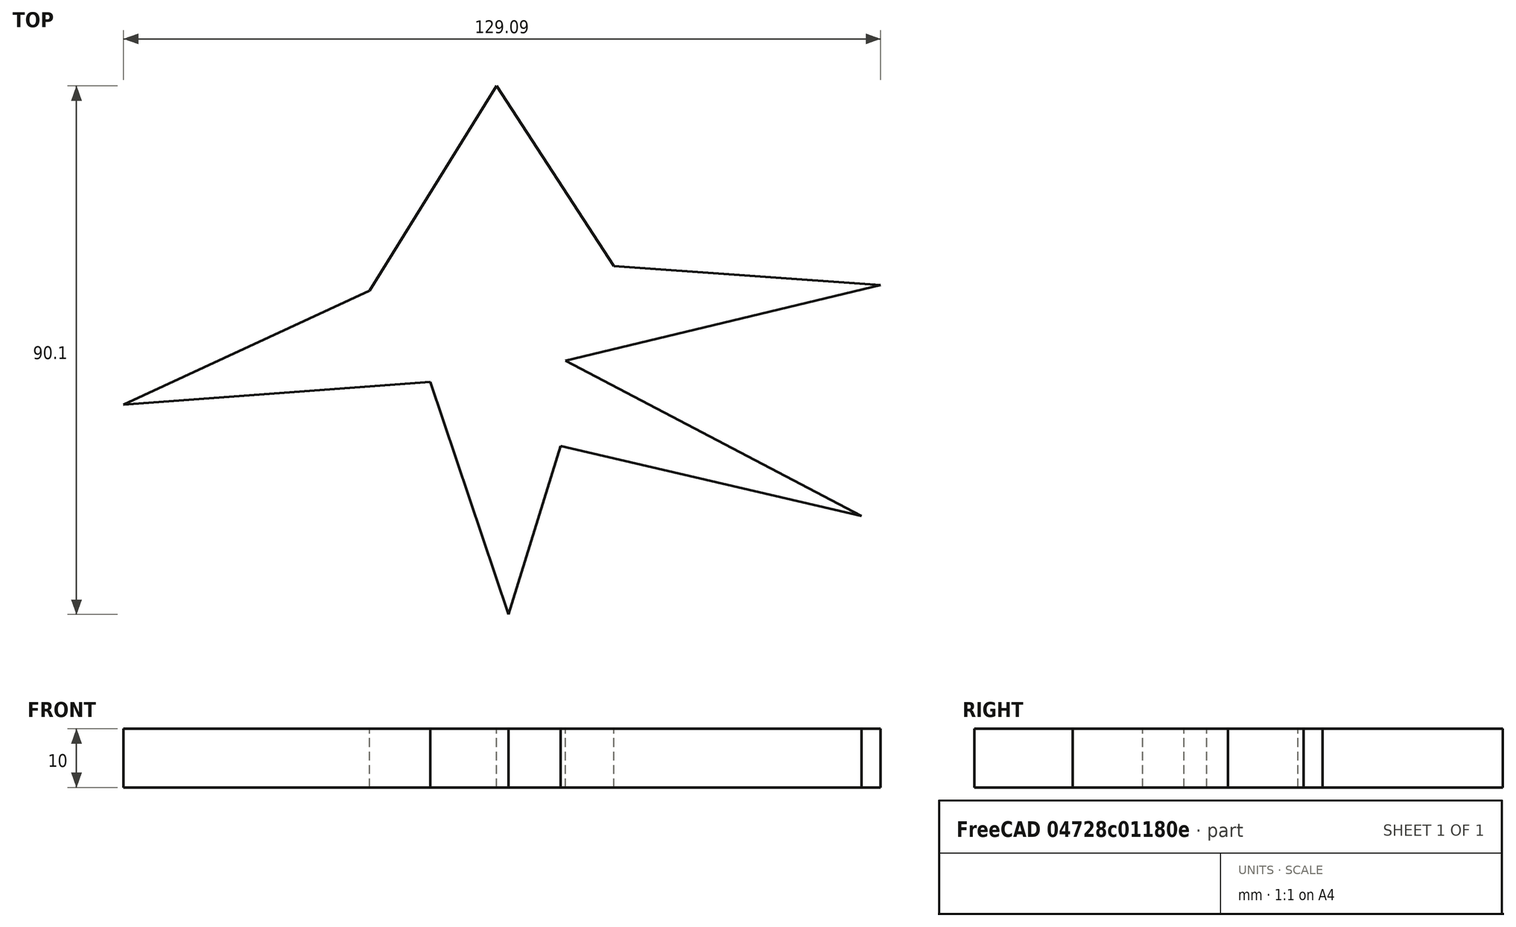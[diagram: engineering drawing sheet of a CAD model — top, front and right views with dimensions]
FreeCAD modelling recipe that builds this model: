
FCSTD DOCUMENT  (FreeCAD 0.21R33694 (Git))
Label: OJT1_T16P01_estrella
License: All rights reserved
LicenseURL: http://en.wikipedia.org/wiki/All_rights_reserved
objects: Sketcher::SketchObject×1, PartDesign::Pad×1, PartDesign::Body×1
note: 4 computed .brp shape members not serialized (recipe doc carries the construction recipe); baked Part::Feature solids carry a one-line shape summary decoded from their .brp

FEATURE [Sketcher::SketchObject] Sketch
  FullyConstrained = false
  MapMode = 5
  Support = -> [XY_Plane]
  sketch-geometry (11):
    g0: LineSegment StartX=-21.6998 StartY=9.21755 StartZ=0 EndX=0.000202475 EndY=44.1413 EndZ=0
    g1: LineSegment StartX=0.000202475 StartY=44.1413 StartZ=0 EndX=20 EndY=13.4343 EndZ=0
    g2: LineSegment StartX=20 StartY=13.4343 StartZ=0 EndX=65.4545 EndY=10.202 EndZ=0
    g3: LineSegment StartX=65.4545 StartY=10.202 StartZ=0 EndX=11.7172 EndY=-2.72727 EndZ=0
    g4: LineSegment StartX=11.7172 StartY=-2.72727 StartZ=0 EndX=62.2222 EndY=-29.1919 EndZ=0
    g5: LineSegment StartX=62.2222 StartY=-29.1919 StartZ=0 EndX=10.9091 EndY=-17.2727 EndZ=0
    g6: LineSegment StartX=10.9091 StartY=-17.2727 StartZ=0 EndX=2.0202 EndY=-45.9596 EndZ=0
    g7: LineSegment StartX=2.0202 StartY=-45.9596 StartZ=0 EndX=-11.3131 EndY=-6.36364 EndZ=0
    g8: LineSegment StartX=-11.3131 StartY=-6.36364 StartZ=0 EndX=-63.6364 EndY=-10.202 EndZ=0
    g9: LineSegment StartX=-63.6364 StartY=-10.202 StartZ=0 EndX=-21.6998 EndY=9.21755 EndZ=0
    g10: GeomPoint X=-21.7946 Y=9.06502 Z=0
  constraints (11):
    c: Coincident(g0,g1)
    c: Coincident(g1,g2)
    c: Coincident(g2,g3)
    c: Coincident(g3,g4)
    c: Coincident(g4,g5)
    c: Coincident(g5,g6)
    c: Coincident(g6,g7)
    c: Coincident(g7,g8)
    c: Coincident(g8,g9)
    c: Coincident(g9,g0)
    c: PointOnObject(g10,g0)
FEATURE [PartDesign::Pad] Pad
  Direction = (0,0,1)
  Length = 10
  Length2 = 10
  Profile = -> Sketch
  ReferenceAxis = -> Sketch [N_Axis]
  Type = 0
FEATURE [PartDesign::Body] Body
  Group = -> [Sketch,Pad]
  Origin = -> Origin
  Tip = -> Pad
